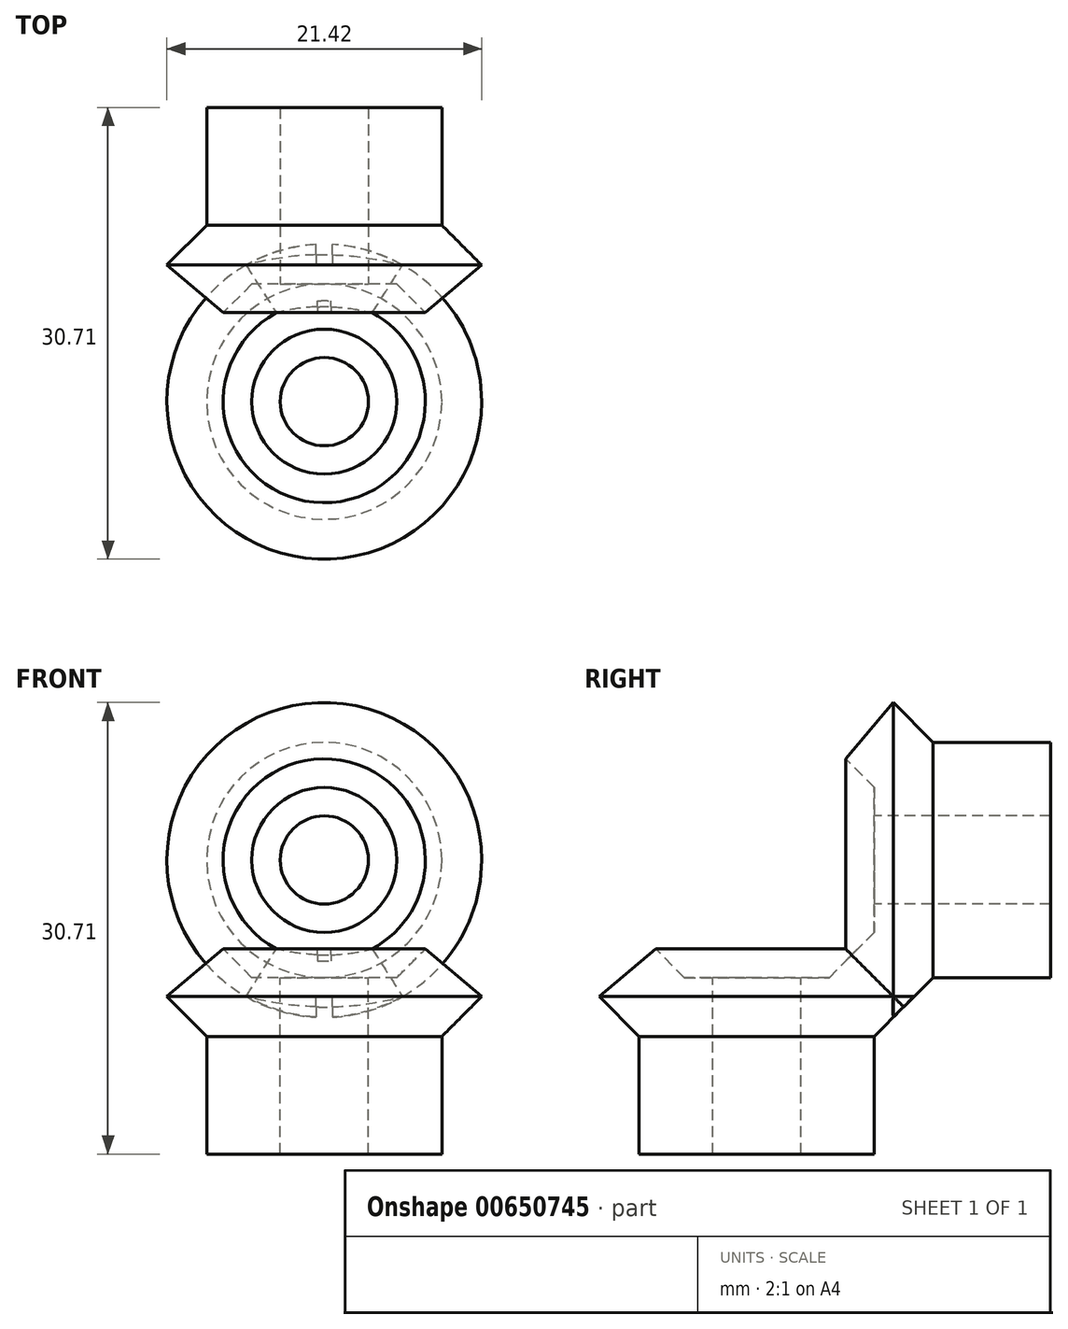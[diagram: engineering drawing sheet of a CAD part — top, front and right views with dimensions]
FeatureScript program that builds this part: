
annotation { "Feature Type Name" : "Feature", "Feature Type Description" : "" }
export const myFeature = defineFeature(function(context is Context, id is Id, definition is map)
    precondition{}
    {
        {
            var Q0;
            Q0=qCreatedBy(makeId("Front.planeOp"),FACE);
            var sketch = newSketch(context, id + "F0", { "sketchPlane" : qUnion([Q0])});
            skLineSegment(sketch, "E0", {"start": v(0, 15.24) * mm, "end": v(0, -22.55) * mm, "construction": true});
            skLineSegment(sketch, "E1", {"start": v(0, 0) * mm, "end": v(-22.2, -19.3) * mm, "construction": true});
            skLineSegment(sketch, "E2", {"start": v(0, -20) * mm, "end": v(-8, -20) * mm});
            skLineSegment(sketch, "E3", {"start": v(-8, -20) * mm, "end": v(-8, -12) * mm});
            skLineSegment(sketch, "E4", {"start": v(-8, -12) * mm, "end": v(-10.7, -9.29) * mm});
            skLineSegment(sketch, "E5", {"start": v(-10.7, -9.3) * mm, "end": v(-6.87, -6.05) * mm});
            skLineSegment(sketch, "E6", {"start": v(-6.88, -6.05) * mm, "end": v(-4.93, -8) * mm});
            skLineSegment(sketch, "E7", {"start": v(-4.93, -8) * mm, "end": v(0, -8) * mm});
            skLineSegment(sketch, "E8", {"start": v(0, -8) * mm, "end": v(0, -20) * mm});
            skSolve(sketch);
        }
        {
            var Q0;
            Q0 = qSketchRegion(id + "F0", true);
            var Q1;
            Q1=sQuery(id+"F0.wireOp",EDGE,"E0");
            revolve(context, id + "F1", {"entities" : qUnion([Q0]), "axis" : qUnion([Q1]), "revolveType" : RevolveType.FULL});
        }
        {
            var Q0;
            Q0=qCreatedBy(makeId("Top.planeOp"),FACE);
            var sketch = newSketch(context, id + "F2", { "sketchPlane" : qUnion([Q0])});
            skCircle(sketch, "E9", {"center": v(0, 0) * mm, "radius": 3 * mm});
            skSolve(sketch);
        }
        {
            var Q0;
            Q0 = qSketchRegion(id + "F2", true);
            extrude(context, id + "F3", {"entities" : qUnion([Q0]), "operationType" : NewBodyOperationType.REMOVE, "endBound" : BoundingType.THROUGH_ALL, "oppositeDirection" : true, "depth" : 25 * mm, "offsetDistance" : 25 * mm});
        }
        {
            var Q0;
            Q0=qCreatedBy(makeId("Front.planeOp"),FACE);
            var sketch = newSketch(context, id + "F4", { "sketchPlane" : qUnion([Q0])});
            skLineSegment(sketch, "E10", {"start": v(-19.88, 0) * mm, "end": v(17.6, 0) * mm, "construction": true});
            skSolve(sketch);
        }
        {
            var Q0;
            Q0=makeQuery(id+"F1.opRevolve","SWEPT_BODY",BODY,{"disambiguationData":[OSD([sQuery(id+"F0.wireOp",EDGE,"E2"),sQuery(id+"F0.wireOp",EDGE,"E3"),sQuery(id+"F0.wireOp",EDGE,"E4"),sQuery(id+"F0.wireOp",EDGE,"E5"),sQuery(id+"F0.wireOp",EDGE,"E6"),sQuery(id+"F0.wireOp",EDGE,"E7"),sQuery(id+"F0.wireOp",EDGE,"E8")])]});
            var Q1;
            Q1=sQuery(id+"F4.wireOp",EDGE,"E10");
            circularPattern(context, id + "F5", {"operationType" : NewBodyOperationType.ADD, "entities" : qUnion([Q0]), "axis" : qUnion([Q1]), "angle" : 90 * degree, "instanceCount" : 2, "equalSpace" : true});
        }
    });
